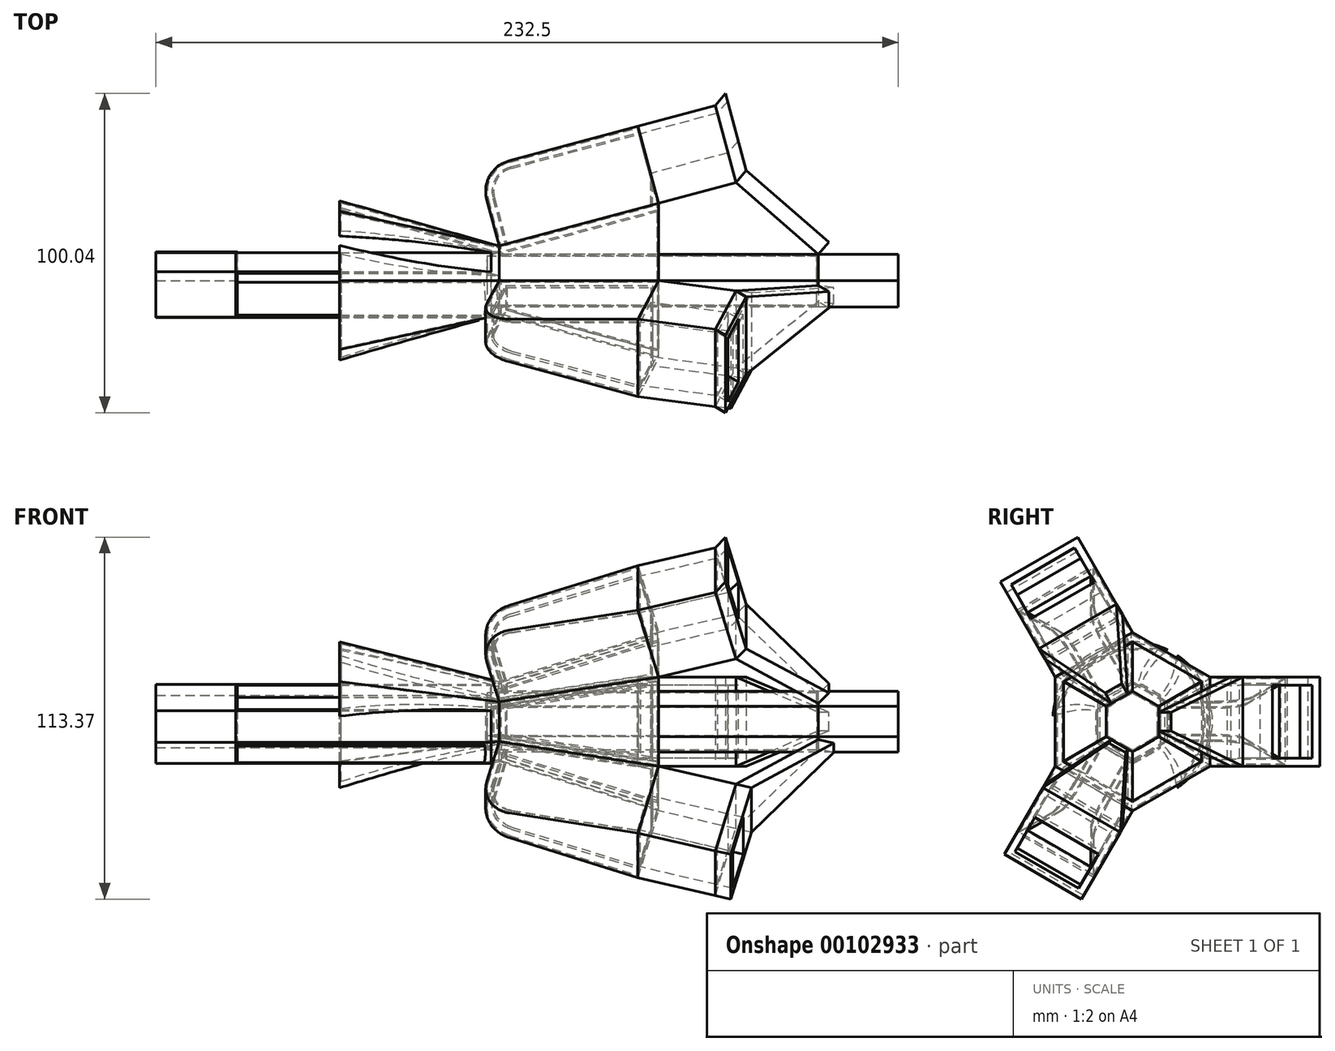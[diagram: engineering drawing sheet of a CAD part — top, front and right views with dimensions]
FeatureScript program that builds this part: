
annotation { "Feature Type Name" : "Feature", "Feature Type Description" : "" }
export const myFeature = defineFeature(function(context is Context, id is Id, definition is map)
    precondition{}
    {
        {
            var Q0;
            Q0=qCreatedBy(makeId("Right.planeOp"),FACE);
            var sketch = newSketch(context, id + "F0", { "sketchPlane" : qUnion([Q0])});
            skCircle(sketch, "E0.cCircle", {"center": v(0, 0) * mm, "radius": 10.83 * mm, "construction": true});
            skLineSegment(sketch, "E0.0", {"start": v(10.83, 6.25) * mm, "end": v(10.83, -6.25) * mm});
            skLineSegment(sketch, "E0.1", {"start": v(10.83, -6.25) * mm, "end": v(0, -12.5) * mm});
            skLineSegment(sketch, "E0.2", {"start": v(0, -12.5) * mm, "end": v(-10.83, -6.25) * mm});
            skLineSegment(sketch, "E0.3", {"start": v(-10.83, -6.25) * mm, "end": v(-10.83, 6.25) * mm});
            skLineSegment(sketch, "E0.4", {"start": v(-10.83, 6.25) * mm, "end": v(0, 12.5) * mm});
            skLineSegment(sketch, "E0.5", {"start": v(0, 12.5) * mm, "end": v(10.83, 6.25) * mm});
            skPoint(sketch, "E0.0.midPoint", {"position": v(10.83, 0) * mm});
            skSolve(sketch);
        }
        {
            var Q0;
            Q0=qCreatedBy(makeId("Right.planeOp"),FACE);
            cPlane(context, id + "F1", {"entities" : qUnion([Q0]), "cplaneType" : CPlaneType.OFFSET, "offset" : 50 * mm, "oppositeDirection" : true, "width" : 150 * mm, "height" : 150 * mm});
        }
        {
            var Q0;
            Q0=qCreatedBy(id+"F1.planeOp",FACE);
            var sketch = newSketch(context, id + "F2", { "sketchPlane" : qUnion([Q0])});
            skCircle(sketch, "E1", {"center": v(0, 0) * mm, "radius": 25 * mm});
            skSolve(sketch);
        }
        {
            var Q0;
            Q0 = qSketchRegion(id + "F2", true);
            var Q1;
            Q1=makeQuery(id+"F0.imprint","IMPRINT",FACE,{"disambiguationData":[TD([[makeQuery(id+"F0.imprint","IMPRINT",EDGE,{"derivedFrom":sQuery(id+"F0.wireOp",EDGE,"E0.0")}),-1.0]])]});
            loft(context, id + "F3", {"sheetProfilesArray" : [{ "sheetProfileEntities" : qUnion([Q0]) }, { "sheetProfileEntities" : qUnion([Q1]) }]});
        }
        {
            var Q0;
            Q0=makeQuery(id+"F3.opLoft","SWEPT_FACE",FACE,{"disambiguationData":[OSD([sQuery(id+"F0.wireOp",EDGE,"E0.0"),sQuery(id+"F0.wireOp",EDGE,"E0.1"),sQuery(id+"F0.wireOp",EDGE,"E0.2"),sQuery(id+"F0.wireOp",EDGE,"E0.3"),sQuery(id+"F2.wireOp",EDGE,"E1")])]});
            var Q1;
            Q1=makeQuery(id+"F3.opLoft","SWEPT_FACE",FACE,{"disambiguationData":[OSD([sQuery(id+"F0.wireOp",EDGE,"E0.2"),sQuery(id+"F0.wireOp",EDGE,"E0.3"),sQuery(id+"F0.wireOp",EDGE,"E0.4"),sQuery(id+"F0.wireOp",EDGE,"E0.5"),sQuery(id+"F2.wireOp",EDGE,"E1")])]});
            var Q2;
            Q2=makeQuery(id+"F3.opLoft","SWEPT_FACE",FACE,{"disambiguationData":[OSD([sQuery(id+"F0.wireOp",EDGE,"E0.0"),sQuery(id+"F0.wireOp",EDGE,"E0.4"),sQuery(id+"F0.wireOp",EDGE,"E0.5"),sQuery(id+"F2.wireOp",EDGE,"E1")])]});
            var Q3;
            Q3=makeQuery(id+"F3.opLoft","CAP_FACE",FACE,{"disambiguationData":[OSD([makeQuery(id+"F2.imprint","IMPRINT",FACE,{"disambiguationData":[TD([[makeQuery(id+"F2.imprint","IMPRINT",EDGE,{"derivedFrom":sQuery(id+"F2.wireOp",EDGE,"E1")}),1.0]])]})])],"isStart":true});
            var Q4;
            Q4=makeQuery(id+"F3.opLoft","SWEPT_BODY",BODY,{"disambiguationData":[OSD([makeQuery(id+"F0.imprint","IMPRINT",FACE,{"disambiguationData":[TD([[makeQuery(id+"F0.imprint","IMPRINT",EDGE,{"derivedFrom":sQuery(id+"F0.wireOp",EDGE,"E0.0")}),-1.0]])]}),makeQuery(id+"F2.imprint","IMPRINT",FACE,{"disambiguationData":[TD([[makeQuery(id+"F2.imprint","IMPRINT",EDGE,{"derivedFrom":sQuery(id+"F2.wireOp",EDGE,"E1")}),1.0]])]})])]});
            shell(context, id + "F4", {"entities" : qUnion([Q0, Q1, Q2, Q3]), "parts" : qUnion([Q4]), "thickness" : 2.5 * mm});
        }
        {
            var Q0;
            Q0=makeQuery(id+"F3.opLoft","CAP_FACE",FACE,{"disambiguationData":[OSD([makeQuery(id+"F0.imprint","IMPRINT",FACE,{"disambiguationData":[TD([[makeQuery(id+"F0.imprint","IMPRINT",EDGE,{"derivedFrom":sQuery(id+"F0.wireOp",EDGE,"E0.0")}),-1.0]])]})])],"isStart":true});
            extrude(context, id + "F5", {"entities" : qUnion([Q0]), "operationType" : NewBodyOperationType.ADD, "depth" : 50 * mm, "hasDraft" : true, "draftAngle" : 15 * degree});
        }
        {
            var Q0;
            Q0=makeQuery(id+"F5.opExtrude","CAP_FACE",FACE,{"disambiguationData":[OSD([makeQuery(id+"F0.imprint","IMPRINT",FACE,{"disambiguationData":[TD([[makeQuery(id+"F0.imprint","IMPRINT",EDGE,{"derivedFrom":sQuery(id+"F0.wireOp",EDGE,"E0.0")}),-1.0]])]})])],"isStart":false});
            shell(context, id + "F18", {"entities" : qUnion([Q0]), "thickness" : 2.5 * mm});
        }
        {
            var Q0;
            Q0=makeQuery(id+"F5.opExtrude","SWEPT_FACE",FACE,{"disambiguationData":[OSD([sQuery(id+"F0.wireOp",EDGE,"E0.0"),sQuery(id+"F0.wireOp",EDGE,"E0.1"),sQuery(id+"F0.wireOp",EDGE,"E0.5")])]});
            extrude(context, id + "F6", {"entities" : qUnion([Q0]), "operationType" : NewBodyOperationType.ADD, "depth" : 25 * mm});
        }
        {
            var Q0;
            Q0=makeQuery(id+"F5.opExtrude","SWEPT_FACE",FACE,{"disambiguationData":[OSD([sQuery(id+"F0.wireOp",EDGE,"E0.3"),sQuery(id+"F0.wireOp",EDGE,"E0.4"),sQuery(id+"F0.wireOp",EDGE,"E0.5")])]});
            extrude(context, id + "F19", {"entities" : qUnion([Q0]), "operationType" : NewBodyOperationType.ADD, "depth" : 25 * mm});
        }
        {
            var Q0;
            Q0=makeQuery(id+"F5.opExtrude","SWEPT_FACE",FACE,{"disambiguationData":[OSD([sQuery(id+"F0.wireOp",EDGE,"E0.1"),sQuery(id+"F0.wireOp",EDGE,"E0.2"),sQuery(id+"F0.wireOp",EDGE,"E0.3")])]});
            extrude(context, id + "F20", {"entities" : qUnion([Q0]), "operationType" : NewBodyOperationType.ADD, "depth" : 25 * mm});
        }
        {
            var Q0;
            Q0=makeQuery(id+"F18.opShell","OFFSET_FACE",FACE,{"disambiguationData":[OSD([makeQuery(id+"F0.imprint","IMPRINT",FACE,{"disambiguationData":[TD([[makeQuery(id+"F0.imprint","IMPRINT",EDGE,{"derivedFrom":sQuery(id+"F0.wireOp",EDGE,"E0.0")}),-1.0]])]})])]});
            extrude(context, id + "F7", {"entities" : qUnion([Q0]), "operationType" : NewBodyOperationType.ADD, "depth" : 100 * mm});
        }
        {
            var Q0;
            {var subQ0=sQuery(id+"F0.wireOp",EDGE,"E0.5");var subQ1=sQuery(id+"F0.wireOp",EDGE,"E0.1");var subQ2=sQuery(id+"F0.wireOp",EDGE,"E0.0");Q0=makeQuery(id+"F6.opExtrude","CAP_EDGE",EDGE,{"disambiguationData":[OSD([subQ2,subQ1,subQ0]),TDD([makeQuery(id+"F5.boolean.opBoolean","MERGE",EDGE,{"derivedFrom":[makeQuery(id+"F3.opLoft","MID_CAP_EDGE",EDGE,{"disambiguationData":[OSD([subQ2,subQ1,subQ0])],"capPos":1.0}),makeQuery(id+"F5.opExtrude","CAP_EDGE",EDGE,{"disambiguationData":[OSD([subQ2,subQ1,subQ0])],"isStart":true})]})])],"isStart":false});}
            var Q1;
            {var subQ0=sQuery(id+"F0.wireOp",EDGE,"E0.5");var subQ1=sQuery(id+"F0.wireOp",EDGE,"E0.4");var subQ2=sQuery(id+"F0.wireOp",EDGE,"E0.3");Q1=makeQuery(id+"F19.opExtrude","CAP_EDGE",EDGE,{"disambiguationData":[OSD([subQ2,subQ1,subQ0]),TDD([makeQuery(id+"F5.boolean.opBoolean","MERGE",EDGE,{"derivedFrom":[makeQuery(id+"F3.opLoft","MID_CAP_EDGE",EDGE,{"disambiguationData":[OSD([subQ2,subQ1,subQ0])],"capPos":1.0}),makeQuery(id+"F5.opExtrude","CAP_EDGE",EDGE,{"disambiguationData":[OSD([subQ2,subQ1,subQ0])],"isStart":true})]})])],"isStart":false});}
            var Q2;
            {var subQ0=sQuery(id+"F0.wireOp",EDGE,"E0.3");var subQ1=sQuery(id+"F0.wireOp",EDGE,"E0.2");var subQ2=sQuery(id+"F0.wireOp",EDGE,"E0.1");Q2=makeQuery(id+"F20.opExtrude","CAP_EDGE",EDGE,{"disambiguationData":[OSD([subQ2,subQ1,subQ0]),TDD([makeQuery(id+"F5.boolean.opBoolean","MERGE",EDGE,{"derivedFrom":[makeQuery(id+"F3.opLoft","MID_CAP_EDGE",EDGE,{"disambiguationData":[OSD([subQ2,subQ1,subQ0])],"capPos":1.0}),makeQuery(id+"F5.opExtrude","CAP_EDGE",EDGE,{"disambiguationData":[OSD([subQ2,subQ1,subQ0])],"isStart":true})]})])],"isStart":false});}
            fillet(context, id + "F8", {"entities" : qUnion([Q0, Q1, Q2]), "radius" : 10 * mm, "tangentPropagation" : true, "allowEdgeOverflow" : false});
        }
        {
            var Q0;
            {var subQ0=sQuery(id+"F0.wireOp",EDGE,"E0.5");var subQ1=sQuery(id+"F0.wireOp",EDGE,"E0.4");var subQ2=sQuery(id+"F0.wireOp",EDGE,"E0.3");Q0=makeQuery(id+"F19.opExtrude","SWEPT_FACE",FACE,{"disambiguationData":[OSD([subQ2,subQ1,subQ0]),TDD([makeQuery(id+"F5.opExtrude","CAP_EDGE",EDGE,{"disambiguationData":[OSD([subQ2,subQ1,subQ0])],"isStart":false})])]});}
            var Q1;
            {var subQ0=sQuery(id+"F0.wireOp",EDGE,"E0.3");var subQ1=sQuery(id+"F0.wireOp",EDGE,"E0.2");var subQ2=sQuery(id+"F0.wireOp",EDGE,"E0.1");Q1=makeQuery(id+"F20.opExtrude","SWEPT_FACE",FACE,{"disambiguationData":[OSD([subQ2,subQ1,subQ0]),TDD([makeQuery(id+"F5.opExtrude","CAP_EDGE",EDGE,{"disambiguationData":[OSD([subQ2,subQ1,subQ0])],"isStart":false})])]});}
            var Q2;
            {var subQ0=sQuery(id+"F0.wireOp",EDGE,"E0.5");var subQ1=sQuery(id+"F0.wireOp",EDGE,"E0.1");var subQ2=sQuery(id+"F0.wireOp",EDGE,"E0.0");Q2=makeQuery(id+"F6.opExtrude","SWEPT_FACE",FACE,{"disambiguationData":[OSD([subQ2,subQ1,subQ0]),TDD([makeQuery(id+"F5.opExtrude","CAP_EDGE",EDGE,{"disambiguationData":[OSD([subQ2,subQ1,subQ0])],"isStart":false})])]});}
            shell(context, id + "F9", {"entities" : qUnion([Q0, Q1, Q2]), "thickness" : 2.5 * mm});
        }
        {
            var Q0;
            Q0=makeQuery(id+"F4.opShell","OFFSET_FACE",FACE,{"disambiguationData":[OSD([makeQuery(id+"F0.imprint","IMPRINT",FACE,{"disambiguationData":[TD([[makeQuery(id+"F0.imprint","IMPRINT",EDGE,{"derivedFrom":sQuery(id+"F0.wireOp",EDGE,"E0.0")}),-1.0]])]})])]});
            extrude(context, id + "F10", {"entities" : qUnion([Q0]), "operationType" : NewBodyOperationType.ADD, "depth" : 80 * mm});
        }
        {
            var Q0;
            Q0=makeQuery(id+"F10.opExtrude","SWEPT_FACE",FACE,{"disambiguationData":[OSD([sQuery(id+"F0.wireOp",EDGE,"E0.1"),sQuery(id+"F0.wireOp",EDGE,"E0.2"),sQuery(id+"F0.wireOp",EDGE,"E0.3")])]});
            var Q1;
            Q1=makeQuery(id+"F10.opExtrude","SWEPT_FACE",FACE,{"disambiguationData":[OSD([sQuery(id+"F0.wireOp",EDGE,"E0.0"),sQuery(id+"F0.wireOp",EDGE,"E0.1"),sQuery(id+"F0.wireOp",EDGE,"E0.5")])]});
            var Q2;
            Q2=makeQuery(id+"F10.opExtrude","SWEPT_FACE",FACE,{"disambiguationData":[OSD([sQuery(id+"F0.wireOp",EDGE,"E0.3"),sQuery(id+"F0.wireOp",EDGE,"E0.4"),sQuery(id+"F0.wireOp",EDGE,"E0.5")])]});
            shell(context, id + "F21", {"entities" : qUnion([Q0, Q1, Q2]), "thickness" : 0.5 * mm});
        }
        {
            var Q0;
            Q0=makeQuery(id+"F10.opExtrude","CAP_FACE",FACE,{"disambiguationData":[OSD([makeQuery(id+"F0.imprint","IMPRINT",FACE,{"disambiguationData":[TD([[makeQuery(id+"F0.imprint","IMPRINT",EDGE,{"derivedFrom":sQuery(id+"F0.wireOp",EDGE,"E0.0")}),-1.0]])]})])],"isStart":false});
            extrude(context, id + "F22", {"entities" : qUnion([Q0]), "depth" : 25 * mm});
        }
        {
            var Q0;
            {var subQ0=sQuery(id+"F0.wireOp",EDGE,"E0.3");var subQ1=sQuery(id+"F0.wireOp",EDGE,"E0.2");var subQ2=sQuery(id+"F0.wireOp",EDGE,"E0.1");Q0=makeQuery(id+"F20.opExtrude","SWEPT_FACE",FACE,{"disambiguationData":[OSD([subQ2,subQ1,subQ0]),TDD([makeQuery(id+"F5.opExtrude","CAP_EDGE",EDGE,{"disambiguationData":[OSD([subQ2,subQ1,subQ0])],"isStart":false})])]});}
            extrude(context, id + "F11", {"entities" : qUnion([Q0]), "depth" : 25 * mm});
        }
        {
            var Q0;
            {var subQ0=sQuery(id+"F0.wireOp",EDGE,"E0.5");var subQ1=sQuery(id+"F0.wireOp",EDGE,"E0.1");var subQ2=sQuery(id+"F0.wireOp",EDGE,"E0.0");Q0=makeQuery(id+"F6.opExtrude","SWEPT_FACE",FACE,{"disambiguationData":[OSD([subQ2,subQ1,subQ0]),TDD([makeQuery(id+"F5.opExtrude","CAP_EDGE",EDGE,{"disambiguationData":[OSD([subQ2,subQ1,subQ0])],"isStart":false})])]});}
            extrude(context, id + "F23", {"entities" : qUnion([Q0]), "depth" : 25 * mm});
        }
        {
            var Q0;
            {var subQ0=sQuery(id+"F0.wireOp",EDGE,"E0.5");var subQ1=sQuery(id+"F0.wireOp",EDGE,"E0.4");var subQ2=sQuery(id+"F0.wireOp",EDGE,"E0.3");Q0=makeQuery(id+"F19.opExtrude","SWEPT_FACE",FACE,{"disambiguationData":[OSD([subQ2,subQ1,subQ0]),TDD([makeQuery(id+"F5.opExtrude","CAP_EDGE",EDGE,{"disambiguationData":[OSD([subQ2,subQ1,subQ0])],"isStart":false})])]});}
            extrude(context, id + "F12", {"entities" : qUnion([Q0]), "depth" : 25 * mm});
        }
        {
            var Q0;
            {var subQ0=sQuery(id+"F0.wireOp",EDGE,"E0.1");var subQ1=sQuery(id+"F0.wireOp",EDGE,"E0.0");var subQ2=sQuery(id+"F0.wireOp",EDGE,"E0.5");Q0=makeQuery(id+"F7.opExtrude","CAP_EDGE",EDGE,{"disambiguationData":[OSD([subQ1,subQ0,subQ2,makeQuery(id+"F0.imprint","IMPRINT",FACE,{"disambiguationData":[TD([[makeQuery(id+"F0.imprint","IMPRINT",EDGE,{"derivedFrom":subQ1}),-1.0]])]})])],"isStart":false});}
            var Q1;
            {var subQ0=sQuery(id+"F0.wireOp",EDGE,"E0.5");var subQ1=sQuery(id+"F0.wireOp",EDGE,"E0.1");var subQ2=sQuery(id+"F0.wireOp",EDGE,"E0.0");var subQ3=makeQuery(id+"F5.opExtrude","CAP_EDGE",EDGE,{"disambiguationData":[OSD([subQ2,subQ1,subQ0])],"isStart":false});Q1=makeQuery(id+"F23.opExtrude","CAP_EDGE",EDGE,{"disambiguationData":[OSD([subQ2,subQ1,subQ0]),TDD([makeQuery(id+"F6.boolean.opBoolean","MERGE",EDGE,{"derivedFrom":[subQ3,makeQuery(id+"F6.opExtrude","CAP_EDGE",EDGE,{"disambiguationData":[OSD([subQ2,subQ1,subQ0]),TDD([subQ3])],"isStart":true})]})])],"isStart":false});}
            loft(context, id + "F24", {"bodyType" : ToolBodyType.SURFACE, "wireProfilesArray" : [{ "wireProfileEntities" : qUnion([Q0]) }, { "wireProfileEntities" : qUnion([Q1]) }]});
        }
        {
            var Q0;
            {var subQ0=sQuery(id+"F0.wireOp",EDGE,"E0.3");var subQ1=sQuery(id+"F0.wireOp",EDGE,"E0.2");var subQ2=sQuery(id+"F0.wireOp",EDGE,"E0.1");Q0=makeQuery(id+"F7.opExtrude","CAP_EDGE",EDGE,{"disambiguationData":[OSD([subQ2,subQ1,subQ0,makeQuery(id+"F0.imprint","IMPRINT",FACE,{"disambiguationData":[TD([[makeQuery(id+"F0.imprint","IMPRINT",EDGE,{"derivedFrom":sQuery(id+"F0.wireOp",EDGE,"E0.0")}),-1.0]])]})])],"isStart":false});}
            var Q1;
            {var subQ0=sQuery(id+"F0.wireOp",EDGE,"E0.3");var subQ1=sQuery(id+"F0.wireOp",EDGE,"E0.2");var subQ2=sQuery(id+"F0.wireOp",EDGE,"E0.1");var subQ3=makeQuery(id+"F5.opExtrude","CAP_EDGE",EDGE,{"disambiguationData":[OSD([subQ2,subQ1,subQ0])],"isStart":false});Q1=makeQuery(id+"F11.opExtrude","CAP_EDGE",EDGE,{"disambiguationData":[OSD([subQ2,subQ1,subQ0]),TDD([makeQuery(id+"F20.boolean.opBoolean","MERGE",EDGE,{"derivedFrom":[subQ3,makeQuery(id+"F20.opExtrude","CAP_EDGE",EDGE,{"disambiguationData":[OSD([subQ2,subQ1,subQ0]),TDD([subQ3])],"isStart":true})]})])],"isStart":false});}
            loft(context, id + "F13", {"bodyType" : ToolBodyType.SURFACE, "wireProfilesArray" : [{ "wireProfileEntities" : qUnion([Q0]) }, { "wireProfileEntities" : qUnion([Q1]) }]});
        }
        {
            var Q0;
            {var subQ0=sQuery(id+"F0.wireOp",EDGE,"E0.3");var subQ1=sQuery(id+"F0.wireOp",EDGE,"E0.4");var subQ2=sQuery(id+"F0.wireOp",EDGE,"E0.5");Q0=makeQuery(id+"F7.opExtrude","CAP_EDGE",EDGE,{"disambiguationData":[OSD([subQ0,subQ1,subQ2,makeQuery(id+"F0.imprint","IMPRINT",FACE,{"disambiguationData":[TD([[makeQuery(id+"F0.imprint","IMPRINT",EDGE,{"derivedFrom":sQuery(id+"F0.wireOp",EDGE,"E0.0")}),-1.0]])]})])],"isStart":false});}
            var Q1;
            {var subQ0=sQuery(id+"F0.wireOp",EDGE,"E0.5");var subQ1=sQuery(id+"F0.wireOp",EDGE,"E0.4");var subQ2=sQuery(id+"F0.wireOp",EDGE,"E0.3");var subQ3=makeQuery(id+"F5.opExtrude","CAP_EDGE",EDGE,{"disambiguationData":[OSD([subQ2,subQ1,subQ0])],"isStart":false});Q1=makeQuery(id+"F12.opExtrude","CAP_EDGE",EDGE,{"disambiguationData":[OSD([subQ2,subQ1,subQ0]),TDD([makeQuery(id+"F19.boolean.opBoolean","MERGE",EDGE,{"derivedFrom":[subQ3,makeQuery(id+"F19.opExtrude","CAP_EDGE",EDGE,{"disambiguationData":[OSD([subQ2,subQ1,subQ0]),TDD([subQ3])],"isStart":true})]})])],"isStart":false});}
            loft(context, id + "F14", {"bodyType" : ToolBodyType.SURFACE, "wireProfilesArray" : [{ "wireProfileEntities" : qUnion([Q0]) }, { "wireProfileEntities" : qUnion([Q1]) }]});
        }
        {
            var Q0;
            Q0=makeQuery(id+"F11.opExtrude","CAP_FACE",FACE,{"disambiguationData":[OSD([sQuery(id+"F0.wireOp",EDGE,"E0.1"),sQuery(id+"F0.wireOp",EDGE,"E0.2"),sQuery(id+"F0.wireOp",EDGE,"E0.3")])],"isStart":false});
            var Q1;
            {var subQ0=sQuery(id+"F0.wireOp",EDGE,"E0.3");var subQ1=sQuery(id+"F0.wireOp",EDGE,"E0.2");var subQ2=sQuery(id+"F0.wireOp",EDGE,"E0.1");var subQ3=sQuery(id+"F0.wireOp",EDGE,"E0.4");Q1=makeQuery(id+"F13.opLoft","SWEPT_FACE",FACE,{"disambiguationData":[OSD([subQ2,subQ1,subQ0,subQ3,makeQuery(id+"F0.imprint","IMPRINT",FACE,{"disambiguationData":[TD([[makeQuery(id+"F0.imprint","IMPRINT",EDGE,{"derivedFrom":sQuery(id+"F0.wireOp",EDGE,"E0.0")}),-1.0]])]}),sQuery(id+"F2.wireOp",EDGE,"E1")])]});}
            extrude(context, id + "F15", {"entities" : qUnion([Q0, Q1]), "depth" : 5 * mm});
        }
        {
            var Q0;
            {var subQ0=sQuery(id+"F0.wireOp",EDGE,"E0.3");var subQ1=sQuery(id+"F0.wireOp",EDGE,"E0.0");var subQ2=sQuery(id+"F0.wireOp",EDGE,"E0.4");var subQ3=sQuery(id+"F0.wireOp",EDGE,"E0.5");Q0=makeQuery(id+"F14.opLoft","SWEPT_FACE",FACE,{"disambiguationData":[OSD([subQ1,subQ0,subQ2,subQ3,makeQuery(id+"F0.imprint","IMPRINT",FACE,{"disambiguationData":[TD([[makeQuery(id+"F0.imprint","IMPRINT",EDGE,{"derivedFrom":subQ1}),-1.0]])]}),sQuery(id+"F2.wireOp",EDGE,"E1")])]});}
            var Q1;
            Q1=makeQuery(id+"F12.opExtrude","CAP_FACE",FACE,{"disambiguationData":[OSD([sQuery(id+"F0.wireOp",EDGE,"E0.3"),sQuery(id+"F0.wireOp",EDGE,"E0.4"),sQuery(id+"F0.wireOp",EDGE,"E0.5")])],"isStart":false});
            extrude(context, id + "F16", {"entities" : qUnion([Q0, Q1]), "oppositeDirection" : true, "depth" : 5 * mm});
        }
        {
            var Q0;
            {var subQ0=sQuery(id+"F0.wireOp",EDGE,"E0.2");var subQ1=sQuery(id+"F0.wireOp",EDGE,"E0.1");var subQ2=sQuery(id+"F0.wireOp",EDGE,"E0.0");var subQ3=sQuery(id+"F0.wireOp",EDGE,"E0.5");Q0=makeQuery(id+"F24.opLoft","SWEPT_FACE",FACE,{"disambiguationData":[OSD([subQ2,subQ1,subQ0,subQ3,makeQuery(id+"F0.imprint","IMPRINT",FACE,{"disambiguationData":[TD([[makeQuery(id+"F0.imprint","IMPRINT",EDGE,{"derivedFrom":subQ2}),-1.0]])]}),sQuery(id+"F2.wireOp",EDGE,"E1")])]});}
            var Q1;
            Q1=makeQuery(id+"F23.opExtrude","CAP_FACE",FACE,{"disambiguationData":[OSD([sQuery(id+"F0.wireOp",EDGE,"E0.0"),sQuery(id+"F0.wireOp",EDGE,"E0.1"),sQuery(id+"F0.wireOp",EDGE,"E0.5")])],"isStart":false});
            extrude(context, id + "F25", {"entities" : qUnion([Q0, Q1]), "depth" : 5 * mm});
        }
        {
            var Q0;
            Q0=makeQuery(id+"F7.opExtrude","CAP_FACE",FACE,{"disambiguationData":[OSD([makeQuery(id+"F0.imprint","IMPRINT",FACE,{"disambiguationData":[TD([[makeQuery(id+"F0.imprint","IMPRINT",EDGE,{"derivedFrom":sQuery(id+"F0.wireOp",EDGE,"E0.0")}),-1.0]])]})])],"isStart":false});
            extrude(context, id + "F17", {"entities" : qUnion([Q0]), "depth" : 25 * mm});
        }
    });
